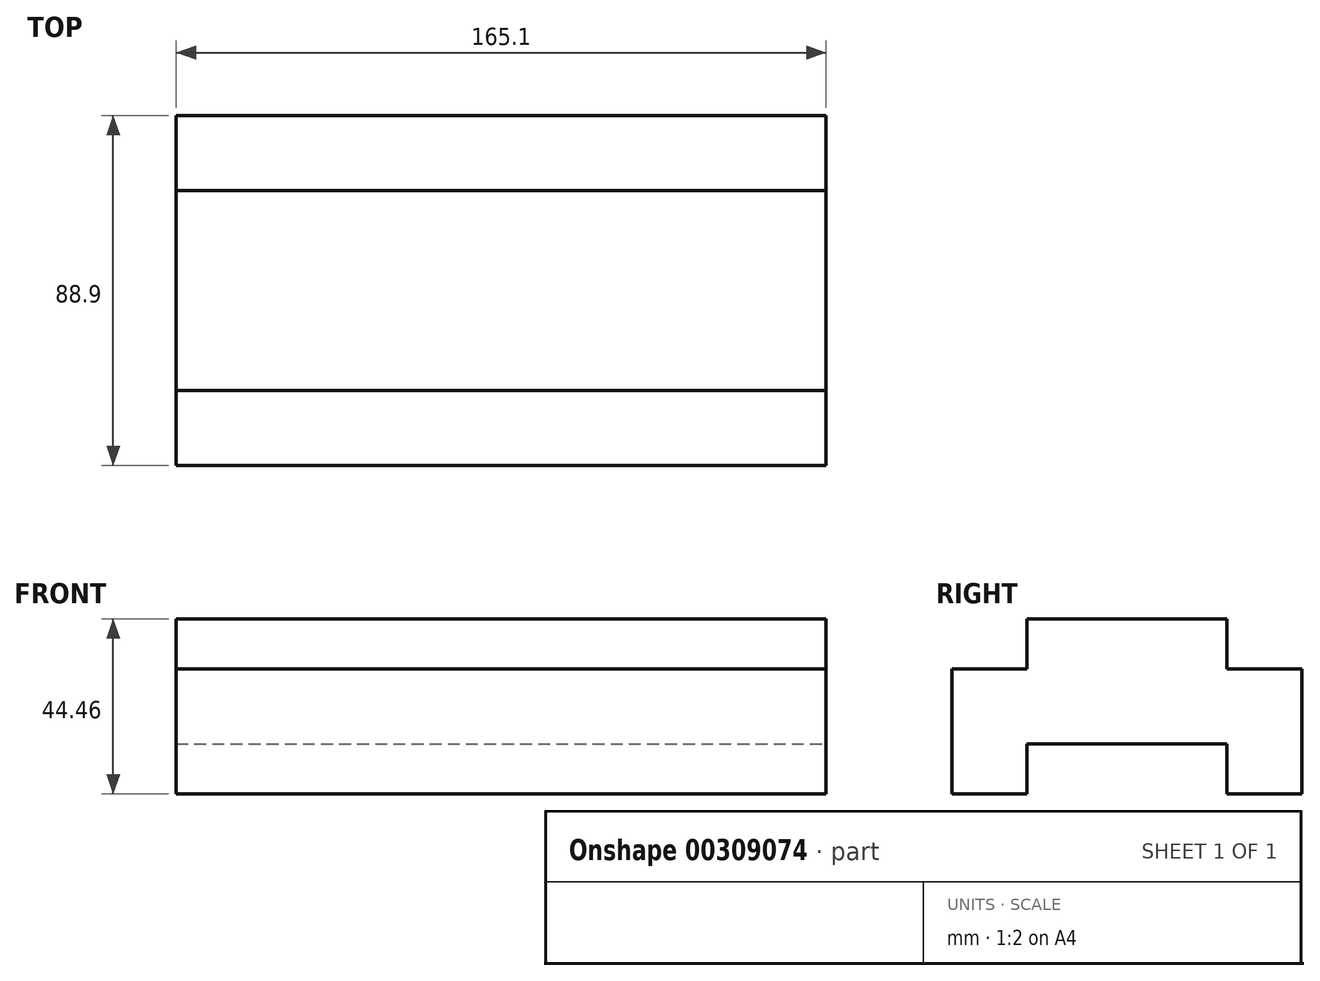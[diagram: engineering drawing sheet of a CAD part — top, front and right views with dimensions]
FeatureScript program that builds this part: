
annotation { "Feature Type Name" : "Feature", "Feature Type Description" : "" }
export const myFeature = defineFeature(function(context is Context, id is Id, definition is map)
    precondition{}
    {
        {
            var Q0;
            Q0=qCreatedBy(makeId("Right.planeOp"),FACE);
            var sketch = newSketch(context, id + "F0", { "sketchPlane" : qUnion([Q0])});
            skLineSegment(sketch, "E0.bottom", {"start": v(-44.45, 22.23) * mm, "end": v(44.45, 22.23) * mm});
            skLineSegment(sketch, "E0.top", {"start": v(-44.45, -22.23) * mm, "end": v(44.45, -22.23) * mm});
            skLineSegment(sketch, "E0.left", {"start": v(-44.45, 22.23) * mm, "end": v(-44.45, -22.23) * mm});
            skLineSegment(sketch, "E0.right", {"start": v(44.45, 22.23) * mm, "end": v(44.45, -22.23) * mm});
            skPoint(sketch, "E0.middle", {"position": v(0, 0) * mm});
            skSolve(sketch);
        }
        {
            var Q0;
            Q0 = qSketchRegion(id + "F0", true);
            extrude(context, id + "F1", {"entities" : qUnion([Q0]), "depth" : 165.1 * mm});
        }
        {
            var Q0;
            Q0=makeQuery(id+"F1.opExtrude","CAP_FACE",FACE,{"disambiguationData":[OSD([sQuery(id+"F0.wireOp",EDGE,"E0.bottom"),sQuery(id+"F0.wireOp",EDGE,"E0.top"),sQuery(id+"F0.wireOp",EDGE,"E0.left"),sQuery(id+"F0.wireOp",EDGE,"E0.right")])],"isStart":false});
            var sketch = newSketch(context, id + "F2", { "sketchPlane" : qUnion([Q0])});
            skLineSegment(sketch, "E1", {"start": v(-44.45, -9.52) * mm, "end": v(44.45, -9.52) * mm});
            skLineSegment(sketch, "E2", {"start": v(-44.45, 9.53) * mm, "end": v(44.45, 9.53) * mm});
            skLineSegment(sketch, "E3", {"start": v(-25.4, 22.23) * mm, "end": v(-25.4, -22.23) * mm});
            skLineSegment(sketch, "E4", {"start": v(25.4, 22.23) * mm, "end": v(25.4, -22.23) * mm});
            skSolve(sketch);
        }
        {
            var Q0;
            {var subQ0=sQuery(id+"F2.wireOp",EDGE,"E2");var subQ1=makeQuery(id+"F1.opExtrude","CAP_EDGE",EDGE,{"disambiguationData":[OSD([sQuery(id+"F0.wireOp",EDGE,"E0.left")])],"isStart":false});var subQ2=makeQuery(id+"F2.imprint","INTERSECT",VERTEX,{"derivedFrom":[subQ1,subQ0]});Q0=makeQuery(id+"F2.imprint","IMPRINT",FACE,{"disambiguationData":[TD([[makeQuery(id+"F2.imprint","IMPRINT",EDGE,{"disambiguationData":[TD([[subQ2,-1.0]])],"derivedFrom":subQ0}),1.0]])]});}
            var Q1;
            {var subQ0=sQuery(id+"F2.wireOp",EDGE,"E2");var subQ1=makeQuery(id+"F1.opExtrude","CAP_EDGE",EDGE,{"disambiguationData":[OSD([sQuery(id+"F0.wireOp",EDGE,"E0.right")])],"isStart":false});var subQ2=makeQuery(id+"F2.imprint","INTERSECT",VERTEX,{"derivedFrom":[subQ1,subQ0]});Q1=makeQuery(id+"F2.imprint","IMPRINT",FACE,{"disambiguationData":[TD([[makeQuery(id+"F2.imprint","IMPRINT",EDGE,{"disambiguationData":[TD([[subQ2,1.0]])],"derivedFrom":subQ0}),1.0]])]});}
            var Q2;
            {var subQ0=sQuery(id+"F2.wireOp",EDGE,"E3");var subQ1=sQuery(id+"F2.wireOp",EDGE,"E1");var subQ2=makeQuery(id+"F2.imprint","INTERSECT",VERTEX,{"derivedFrom":[subQ1,subQ0]});Q2=makeQuery(id+"F2.imprint","IMPRINT",FACE,{"disambiguationData":[TD([[makeQuery(id+"F2.imprint","IMPRINT",EDGE,{"disambiguationData":[TD([[subQ2,-1.0]])],"derivedFrom":subQ1}),-1.0]])]});}
            extrude(context, id + "F3", {"entities" : qUnion([Q0, Q1, Q2]), "operationType" : NewBodyOperationType.REMOVE, "oppositeDirection" : true, "depth" : 165.1 * mm});
        }
    });
